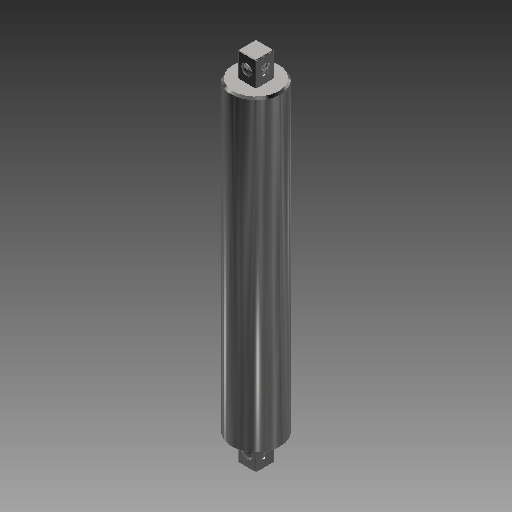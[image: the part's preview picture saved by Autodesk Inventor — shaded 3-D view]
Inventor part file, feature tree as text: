
AUTODESK INVENTOR PART (.ipt)
format: ipt  version: 2019 (Build 230136000, 136)  size: 172,544 bytes
history: native  units: mm
features: sketch x3, extrude x2, split x2, fillet x1, revolve x1, mirror x1, chamfer x1, plane x1, projected_geometry x1
ambient origin geometry x8: Origin, YZ Plane, XZ Plane, XY Plane, X Axis, Y Axis, Z Axis, Center Point
bodies: Solid1 (feature_tree)
feature tree (13):
  extrude  "Extrusion1"  Depth=50.0mm TaperAngle=0.0deg
  extrude  "Extrusion2"  Depth=3.0mm
  fillet  "Fillet1"  Radius=1.5mm
  revolve  "Revolution1"  [1 undecoded]
  mirror  "Mirror1"
  chamfer  "Chamfer2"  Distance=0.2mm
  plane  "Work Plane1"
  split  "Split1"
  split  "Split2"
  sketch  "Sketch1"  dims[d0=8.0mm d1=50.0mm d2=0.0mm]
  sketch  "Sketch2"  dims[d3=3.0mm d4=3.0mm d5=1.5mm]
  sketch  "Sketch3"  dims[d6=1.5mm d7=4.0mm d8=0.0mm d9=0.2mm d10=1.75mm d11=3.5mm d12=90.0deg d16=0.3mm d17=2.0mm d18=45.0deg d19=-50.5mm]
  projected_geometry  "Project Cut Edges1"
note: 1 required parameter value undecoded (feature->parameter linkage not recoverable at this tier; creation-order binding heuristic only, values carry confidence <= 0.55)
